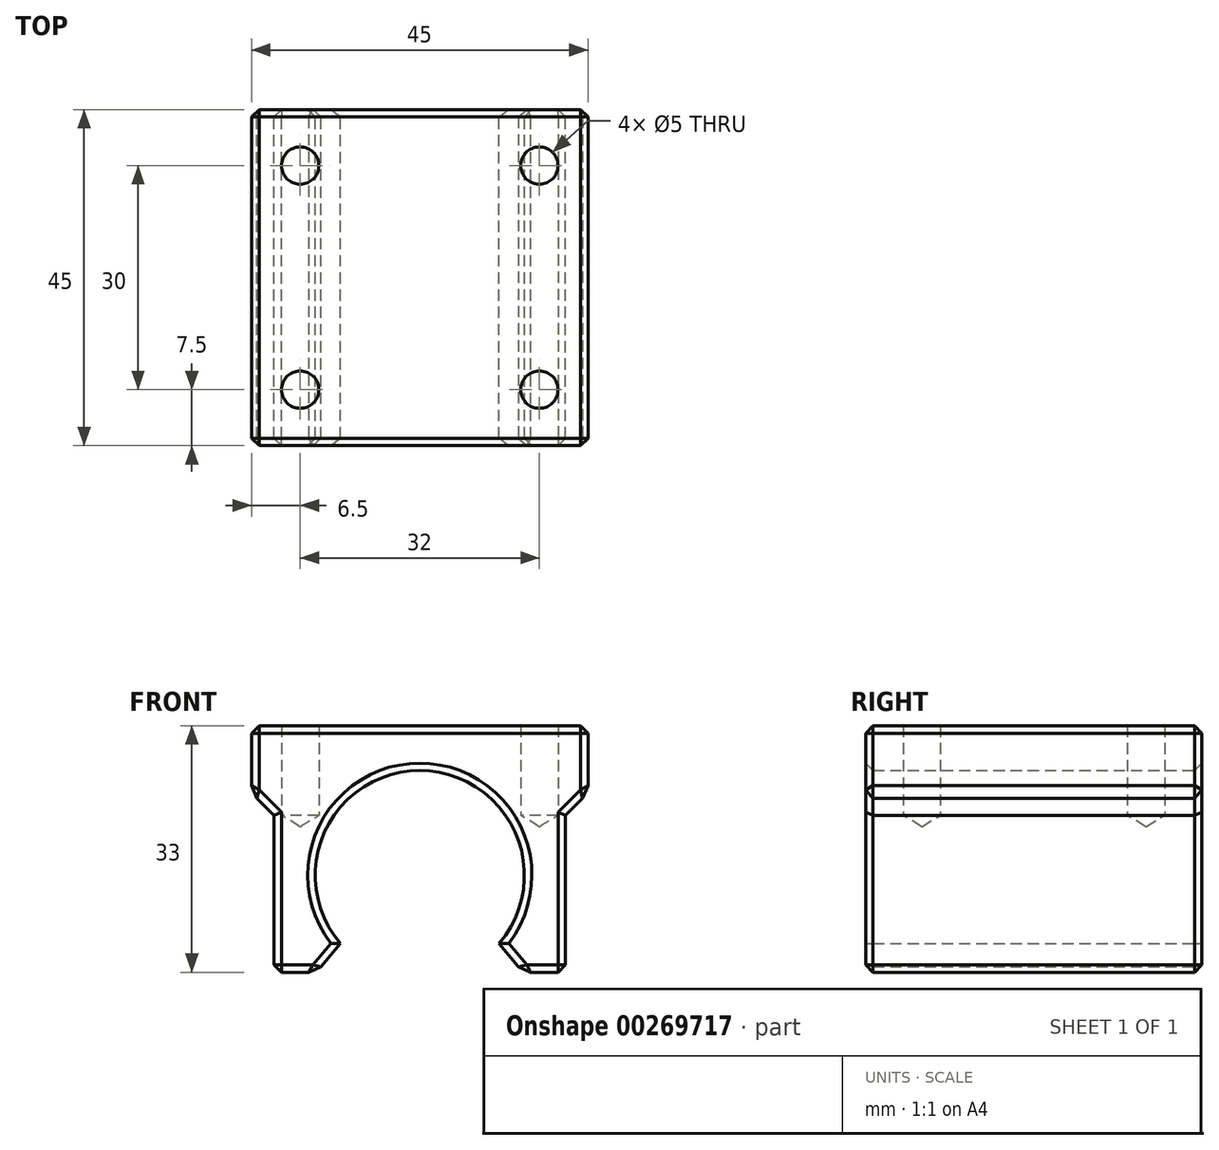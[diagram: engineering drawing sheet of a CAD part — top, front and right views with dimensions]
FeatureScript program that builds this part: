
annotation { "Feature Type Name" : "Feature", "Feature Type Description" : "" }
export const myFeature = defineFeature(function(context is Context, id is Id, definition is map)
    precondition{}
    {
        {
            var Q0;
            Q0=qCreatedBy(makeId("Front.planeOp"),FACE);
            var sketch = newSketch(context, id + "F0", { "sketchPlane" : qUnion([Q0])});
            skLineSegment(sketch, "E0.bottom", {"start": v(22.5, 16.5) * mm, "end": v(-22.5, 16.5) * mm});
            skLineSegment(sketch, "E0.top", {"start": v(19.5, -16.5) * mm, "end": v(13.85, -16.5) * mm});
            skLineSegment(sketch, "E0.left", {"start": v(22.5, 16.5) * mm, "end": v(22.5, 7.5) * mm});
            skLineSegment(sketch, "E0.right", {"start": v(-22.5, 16.5) * mm, "end": v(-22.5, 7.5) * mm});
            skPoint(sketch, "E0.middle", {"position": v(0, 0) * mm});
            skArc(sketch, "E1", {"start": v(10.6, -12.64) * mm, "mid": v(0, 10.5) * mm, "end": v(-10.6, -12.64) * mm});
            skLineSegment(sketch, "E2", {"start": v(-13.85, -16.5) * mm, "end": v(-10.6, -12.64) * mm});
            skLineSegment(sketch, "E3", {"start": v(13.85, -16.5) * mm, "end": v(10.6, -12.64) * mm});
            skLineSegment(sketch, "E4.trimOffspring", {"start": v(-13.85, -16.5) * mm, "end": v(-19.5, -16.5) * mm});
            skLineSegment(sketch, "E5", {"start": v(-22.5, 7.5) * mm, "end": v(-19.5, 4.5) * mm});
            skLineSegment(sketch, "E6", {"start": v(-19.5, 4.5) * mm, "end": v(-19.5, -16.5) * mm});
            skLineSegment(sketch, "E7", {"start": v(22.5, 7.5) * mm, "end": v(19.5, 4.5) * mm});
            skLineSegment(sketch, "E8", {"start": v(19.5, 4.5) * mm, "end": v(19.5, -16.5) * mm});
            skPoint(sketch, "E9.orphan", {"position": v(-22.5, -16.5) * mm});
            skPoint(sketch, "E10.orphan", {"position": v(22.5, -16.5) * mm});
            skSolve(sketch);
        }
        {
            var Q0;
            Q0=makeQuery(id+"F0.imprint","IMPRINT",FACE,{"disambiguationData":[TD([[makeQuery(id+"F0.imprint","IMPRINT",EDGE,{"derivedFrom":sQuery(id+"F0.wireOp",EDGE,"E0.bottom")}),1.0]])]});
            extrude(context, id + "F1", {"entities" : qUnion([Q0]), "depth" : 45 * mm});
        }
        {
            var Q0;
            Q0=makeQuery(id+"F1.opExtrude","SWEPT_FACE",FACE,{"disambiguationData":[OSD([sQuery(id+"F0.wireOp",EDGE,"E0.bottom")])]});
            var sketch = newSketch(context, id + "F2", { "sketchPlane" : qUnion([Q0])});
            skPoint(sketch, "E11", {"position": v(-16, -7.5) * mm});
            skPoint(sketch, "E12", {"position": v(-16, -37.5) * mm});
            skPoint(sketch, "E13", {"position": v(16, -37.5) * mm});
            skPoint(sketch, "E14", {"position": v(16, -7.5) * mm});
            skLineSegment(sketch, "E15", {"start": v(-22.5, -22.5) * mm, "end": v(22.5, -22.5) * mm, "construction": true});
            skSolve(sketch);
        }
        {
            var Q0;
            Q0=sQuery(id+"F2.wireOp",VERTEX,"E11");
            var Q1;
            Q1=sQuery(id+"F2.wireOp",VERTEX,"E14");
            var Q2;
            Q2=sQuery(id+"F2.wireOp",VERTEX,"E13");
            var Q3;
            Q3=sQuery(id+"F2.wireOp",VERTEX,"E12");
            var Q4;
            Q4=makeQuery(id+"F1.opExtrude","SWEPT_BODY",BODY,{"disambiguationData":[OSD([sQuery(id+"F0.wireOp",EDGE,"E0.bottom"),sQuery(id+"F0.wireOp",EDGE,"E0.top"),sQuery(id+"F0.wireOp",EDGE,"E0.left"),sQuery(id+"F0.wireOp",EDGE,"E0.right"),sQuery(id+"F0.wireOp",EDGE,"E1"),sQuery(id+"F0.wireOp",EDGE,"E2"),sQuery(id+"F0.wireOp",EDGE,"E3"),sQuery(id+"F0.wireOp",EDGE,"E4.trimOffspring")])]});
            hole(context, id + "F3", {"style" : HoleStyle.SIMPLE, "endStyle" : HoleEndStyle.BLIND, "holeDiameter" : 5 * mm, "holeDepth" : 12 * mm, "locations" : qUnion([Q0, Q1, Q2, Q3]), "scope" : qUnion([Q4]), "tappedDepth" : 12 * mm, "tapClearance" : 3, "startStyle" : HoleStartStyle.PART});
        }
        {
            var Q0;
            Q0=makeQuery(id+"F1.opExtrude","CAP_FACE",FACE,{"disambiguationData":[OSD([sQuery(id+"F0.wireOp",EDGE,"E0.bottom"),sQuery(id+"F0.wireOp",EDGE,"E0.top"),sQuery(id+"F0.wireOp",EDGE,"E0.left"),sQuery(id+"F0.wireOp",EDGE,"E0.right"),sQuery(id+"F0.wireOp",EDGE,"E1"),sQuery(id+"F0.wireOp",EDGE,"E2"),sQuery(id+"F0.wireOp",EDGE,"E3"),sQuery(id+"F0.wireOp",EDGE,"E4.trimOffspring")])],"isStart":true});
            var Q1;
            Q1=makeQuery(id+"F1.opExtrude","SWEPT_FACE",FACE,{"disambiguationData":[OSD([sQuery(id+"F0.wireOp",EDGE,"E0.right")])]});
            var Q2;
            Q2=makeQuery(id+"F1.opExtrude","CAP_FACE",FACE,{"disambiguationData":[OSD([sQuery(id+"F0.wireOp",EDGE,"E0.bottom"),sQuery(id+"F0.wireOp",EDGE,"E0.top"),sQuery(id+"F0.wireOp",EDGE,"E0.left"),sQuery(id+"F0.wireOp",EDGE,"E0.right"),sQuery(id+"F0.wireOp",EDGE,"E1"),sQuery(id+"F0.wireOp",EDGE,"E2"),sQuery(id+"F0.wireOp",EDGE,"E3"),sQuery(id+"F0.wireOp",EDGE,"E4.trimOffspring")])],"isStart":false});
            var Q3;
            Q3=makeQuery(id+"F1.opExtrude","SWEPT_FACE",FACE,{"disambiguationData":[OSD([sQuery(id+"F0.wireOp",EDGE,"E4.trimOffspring")])]});
            var Q4;
            Q4=makeQuery(id+"F1.opExtrude","SWEPT_FACE",FACE,{"disambiguationData":[OSD([sQuery(id+"F0.wireOp",EDGE,"E0.top")])]});
            var Q5;
            Q5=makeQuery(id+"F1.opExtrude","SWEPT_FACE",FACE,{"disambiguationData":[OSD([sQuery(id+"F0.wireOp",EDGE,"E0.left")])]});
            chamfer(context, id + "F4", {"entities" : qUnion([Q0, Q1, Q2, Q3, Q4, Q5]), "width" : 1 * mm, "tangentPropagation" : true});
        }
    });
